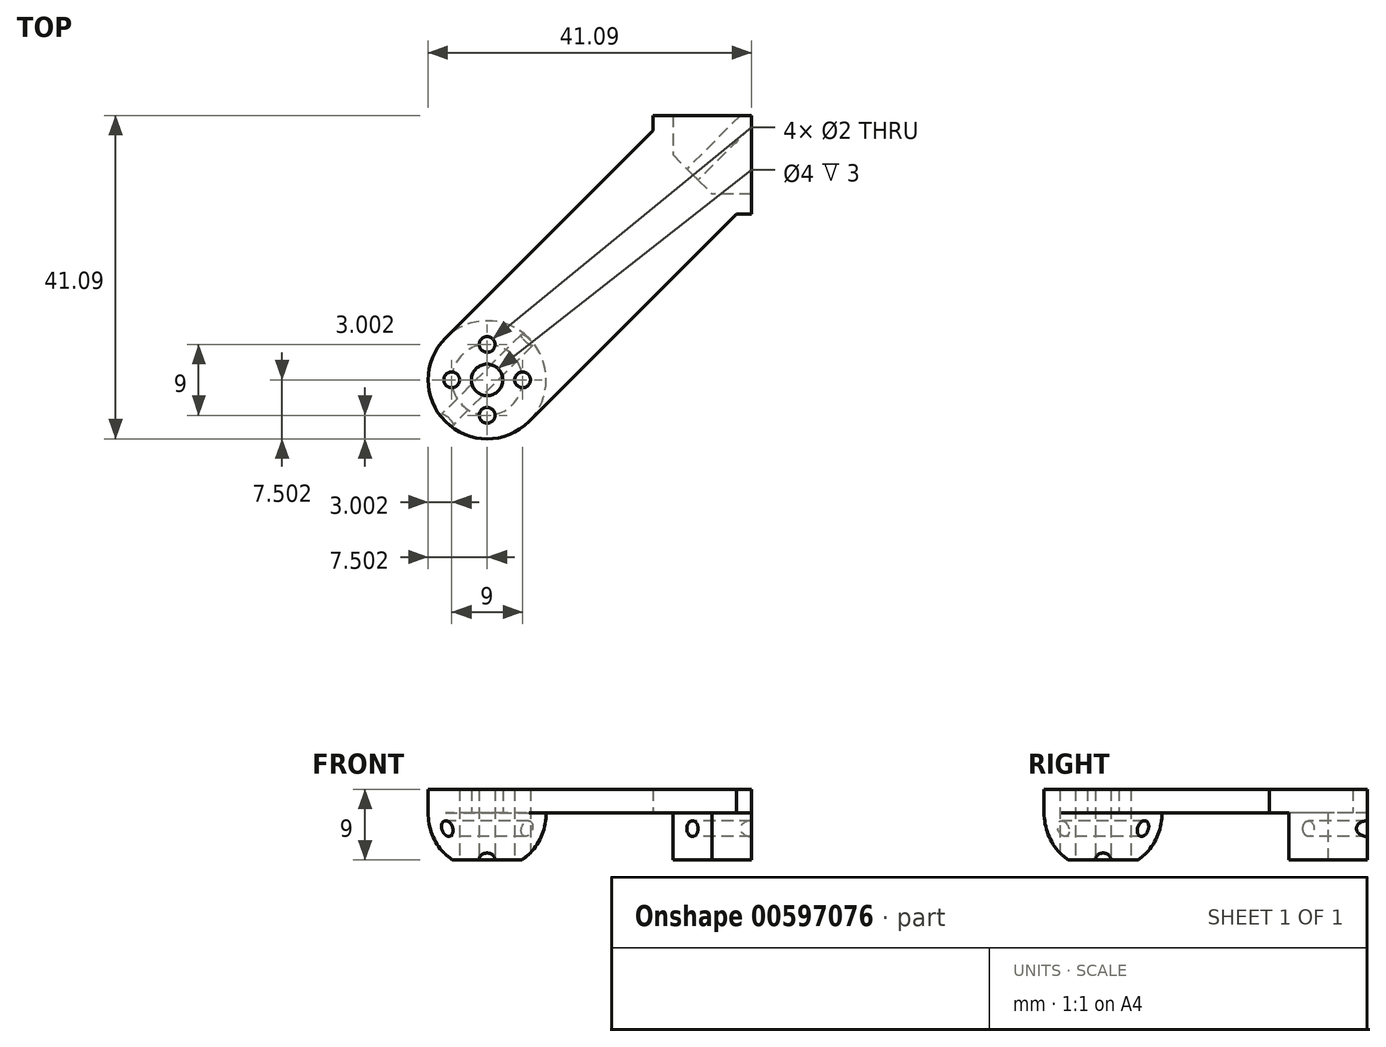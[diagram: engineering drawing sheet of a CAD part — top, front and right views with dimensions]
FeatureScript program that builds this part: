
annotation { "Feature Type Name" : "Feature", "Feature Type Description" : "" }
export const myFeature = defineFeature(function(context is Context, id is Id, definition is map)
    precondition{}
    {
        {
            var Q0;
            Q0=qCreatedBy(makeId("Top.planeOp"),FACE);
            var sketch = newSketch(context, id + "F0", { "sketchPlane" : qUnion([Q0])});
            skLineSegment(sketch, "E0.bottom", {"start": v(0, 0) * mm, "end": v(-12.5, 0) * mm});
            skLineSegment(sketch, "E0.top", {"start": v(0, -12.5) * mm, "end": v(-1.9, -12.5) * mm});
            skLineSegment(sketch, "E0.left", {"start": v(0, 0) * mm, "end": v(0, -12.5) * mm});
            skLineSegment(sketch, "E0.right", {"start": v(-12.5, 0) * mm, "end": v(-12.5, -1.9) * mm});
            skLineSegment(sketch, "E1", {"start": v(-7.2, -7.2) * mm, "end": v(-33.59, -33.59) * mm, "construction": true});
            skCircle(sketch, "E2", {"center": v(-33.59, -33.59) * mm, "radius": 2 * mm});
            skCircle(sketch, "E3", {"center": v(-33.59, -33.59) * mm, "radius": 4.5 * mm, "construction": true});
            skCircle(sketch, "E4", {"center": v(-33.59, -29.09) * mm, "radius": 1 * mm});
            skCircle(sketch, "E5", {"center": v(-38.09, -33.59) * mm, "radius": 1 * mm});
            skCircle(sketch, "E6", {"center": v(-33.59, -38.09) * mm, "radius": 1 * mm});
            skCircle(sketch, "E7", {"center": v(-29.09, -33.59) * mm, "radius": 1 * mm});
            skLineSegment(sketch, "E8", {"start": v(0, 0) * mm, "end": v(0, -52.07) * mm, "construction": true});
            skLineSegment(sketch, "E9", {"start": v(0, 0) * mm, "end": v(-59.68, 0) * mm, "construction": true});
            skCircle(sketch, "E10", {"center": v(-33.59, -33.59) * mm, "radius": 31.75 * mm, "construction": true});
            skArc(sketch, "E11", {"start": v(-38.9, -28.28) * mm, "mid": v(-38.9, -38.9) * mm, "end": v(-28.28, -38.9) * mm});
            skLineSegment(sketch, "E12", {"start": v(-1.9, -12.5) * mm, "end": v(-28.28, -38.9) * mm});
            skLineSegment(sketch, "E13", {"start": v(-12.5, -1.9) * mm, "end": v(-38.9, -28.28) * mm});
            skSolve(sketch);
        }
        {
            var Q0;
            Q0=makeQuery(id+"F0.imprint","IMPRINT",FACE,{"disambiguationData":[TD([[makeQuery(id+"F0.imprint","IMPRINT",EDGE,{"derivedFrom":sQuery(id+"F0.wireOp",EDGE,"E0.bottom")}),1.0]])]});
            extrude(context, id + "F1", {"entities" : qUnion([Q0]), "depth" : 3 * mm, "offsetDistance" : 25 * mm});
        }
        {
            var Q0;
            Q0=qCreatedBy(makeId("Top.planeOp"),FACE);
            var sketch = newSketch(context, id + "F2", { "sketchPlane" : qUnion([Q0])});
            skLineSegment(sketch, "E14.bottom", {"start": v(0, 0) * mm, "end": v(-10, 0) * mm});
            skLineSegment(sketch, "E14.top", {"start": v(0, -10) * mm, "end": v(-5, -10) * mm});
            skLineSegment(sketch, "E14.left", {"start": v(0, 0) * mm, "end": v(0, -10) * mm});
            skLineSegment(sketch, "E14.right", {"start": v(-10, 0) * mm, "end": v(-10, -5) * mm});
            skLineSegment(sketch, "E15", {"start": v(-10, -5) * mm, "end": v(-5, -10) * mm});
            skLineSegment(sketch, "E16", {"start": v(-28.28, -28.28) * mm, "end": v(-33.59, -33.59) * mm, "construction": true});
            skCircle(sketch, "E17", {"center": v(-33.59, -33.59) * mm, "radius": 7.5 * mm});
            skLineSegment(sketch, "E18", {"start": v(-28.28, -28.28) * mm, "end": v(-38.9, -38.9) * mm});
            skSolve(sketch);
        }
        {
            var Q0;
            {var subQ0=sQuery(id+"F2.wireOp",EDGE,"E18");Q0=makeQuery(id+"F2.imprint","IMPRINT",FACE,{"disambiguationData":[TD([[makeQuery(id+"F2.imprint","IMPRINT",EDGE,{"derivedFrom":subQ0}),-1.0]])]});}
            var Q1;
            Q1=sQuery(id+"F2.wireOp",EDGE,"E18");
            revolve(context, id + "F3", {"operationType" : NewBodyOperationType.ADD, "entities" : qUnion([Q0]), "axis" : qUnion([Q1]), "revolveType" : RevolveType.ONE_DIRECTION, "angle" : 180 * degree});
        }
        {
            var Q0;
            Q0=makeQuery(id+"F0.imprint","IMPRINT",FACE,{"disambiguationData":[TD([[makeQuery(id+"F0.imprint","IMPRINT",EDGE,{"derivedFrom":sQuery(id+"F0.wireOp",EDGE,"E6")}),1.0]])]});
            var Q1;
            Q1=makeQuery(id+"F0.imprint","IMPRINT",FACE,{"disambiguationData":[TD([[makeQuery(id+"F0.imprint","IMPRINT",EDGE,{"derivedFrom":sQuery(id+"F0.wireOp",EDGE,"E7")}),1.0]])]});
            var Q2;
            Q2=makeQuery(id+"F0.imprint","IMPRINT",FACE,{"disambiguationData":[TD([[makeQuery(id+"F0.imprint","IMPRINT",EDGE,{"derivedFrom":sQuery(id+"F0.wireOp",EDGE,"E5")}),1.0]])]});
            var Q3;
            Q3=makeQuery(id+"F0.imprint","IMPRINT",FACE,{"disambiguationData":[TD([[makeQuery(id+"F0.imprint","IMPRINT",EDGE,{"derivedFrom":sQuery(id+"F0.wireOp",EDGE,"E4")}),1.0]])]});
            extrude(context, id + "F4", {"entities" : qUnion([Q0, Q1, Q2, Q3]), "operationType" : NewBodyOperationType.REMOVE, "oppositeDirection" : true, "depth" : 25 * mm, "offsetDistance" : 25 * mm});
        }
        {
            var Q0;
            Q0=makeQuery(id+"F2.imprint","IMPRINT",FACE,{"disambiguationData":[TD([[makeQuery(id+"F2.imprint","IMPRINT",EDGE,{"derivedFrom":sQuery(id+"F2.wireOp",EDGE,"E14.bottom")}),1.0]])]});
            extrude(context, id + "F5", {"entities" : qUnion([Q0]), "operationType" : NewBodyOperationType.ADD, "oppositeDirection" : true, "depth" : 7 * mm, "offsetDistance" : 25 * mm});
        }
        {
            var Q0;
            Q0=makeQuery(id+"F5.opExtrude","SWEPT_FACE",FACE,{"disambiguationData":[OSD([sQuery(id+"F2.wireOp",EDGE,"E15")])]});
            var sketch = newSketch(context, id + "F6", { "sketchPlane" : qUnion([Q0])});
            skLineSegment(sketch, "E19", {"start": v(0, 0) * mm, "end": v(0, -2) * mm, "construction": true});
            skPoint(sketch, "E19.endSnap0", {"position": v(0, 0) * mm});
            skCircle(sketch, "E20", {"center": v(0, -2) * mm, "radius": 1 * mm});
            skSolve(sketch);
        }
        {
            var Q0;
            Q0=makeQuery(id+"F6.imprint","IMPRINT",FACE,{"disambiguationData":[TD([[makeQuery(id+"F6.imprint","IMPRINT",EDGE,{"derivedFrom":sQuery(id+"F6.wireOp",EDGE,"E20")}),1.0]])]});
            extrude(context, id + "F7", {"entities" : qUnion([Q0]), "operationType" : NewBodyOperationType.REMOVE, "endBound" : BoundingType.THROUGH_ALL, "oppositeDirection" : true, "depth" : 25 * mm, "offsetDistance" : 25 * mm, "hasSecondDirection" : true, "secondDirectionBound" : SecondDirectionBoundingType.THROUGH_ALL, "secondDirectionOppositeDirection" : false, "secondDirectionDepth" : 25 * mm});
        }
        {
            var Q0;
            Q0=qCreatedBy(makeId("Top.planeOp"),FACE);
            cPlane(context, id + "F8", {"entities" : qUnion([Q0]), "cplaneType" : CPlaneType.OFFSET, "offset" : 6 * mm, "oppositeDirection" : true, "width" : 150 * mm, "height" : 150 * mm});
        }
        {
            var Q0;
            Q0=qCreatedBy(id+"F8.planeOp",FACE);
            var sketch = newSketch(context, id + "F9", { "sketchPlane" : qUnion([Q0])});
            skLineSegment(sketch, "E21.bottom", {"start": v(10.92, 12.56) * mm, "end": v(-45.2, 12.56) * mm});
            skLineSegment(sketch, "E21.top", {"start": v(10.92, -61.3) * mm, "end": v(-45.2, -61.3) * mm});
            skLineSegment(sketch, "E21.left", {"start": v(10.92, 12.56) * mm, "end": v(10.92, -61.3) * mm});
            skLineSegment(sketch, "E21.right", {"start": v(-45.2, 12.56) * mm, "end": v(-45.2, -61.3) * mm});
            skPoint(sketch, "E21.middle", {"position": v(-17.14, -24.37) * mm});
            skSolve(sketch);
        }
        {
            var Q0;
            Q0=makeQuery(id+"F9.imprint","IMPRINT",FACE,{"disambiguationData":[TD([[makeQuery(id+"F9.imprint","IMPRINT",EDGE,{"derivedFrom":sQuery(id+"F9.wireOp",EDGE,"E21.bottom")}),1.0]])]});
            extrude(context, id + "F10", {"entities" : qUnion([Q0]), "operationType" : NewBodyOperationType.REMOVE, "oppositeDirection" : true, "depth" : 25 * mm, "offsetDistance" : 25 * mm});
        }
    });
